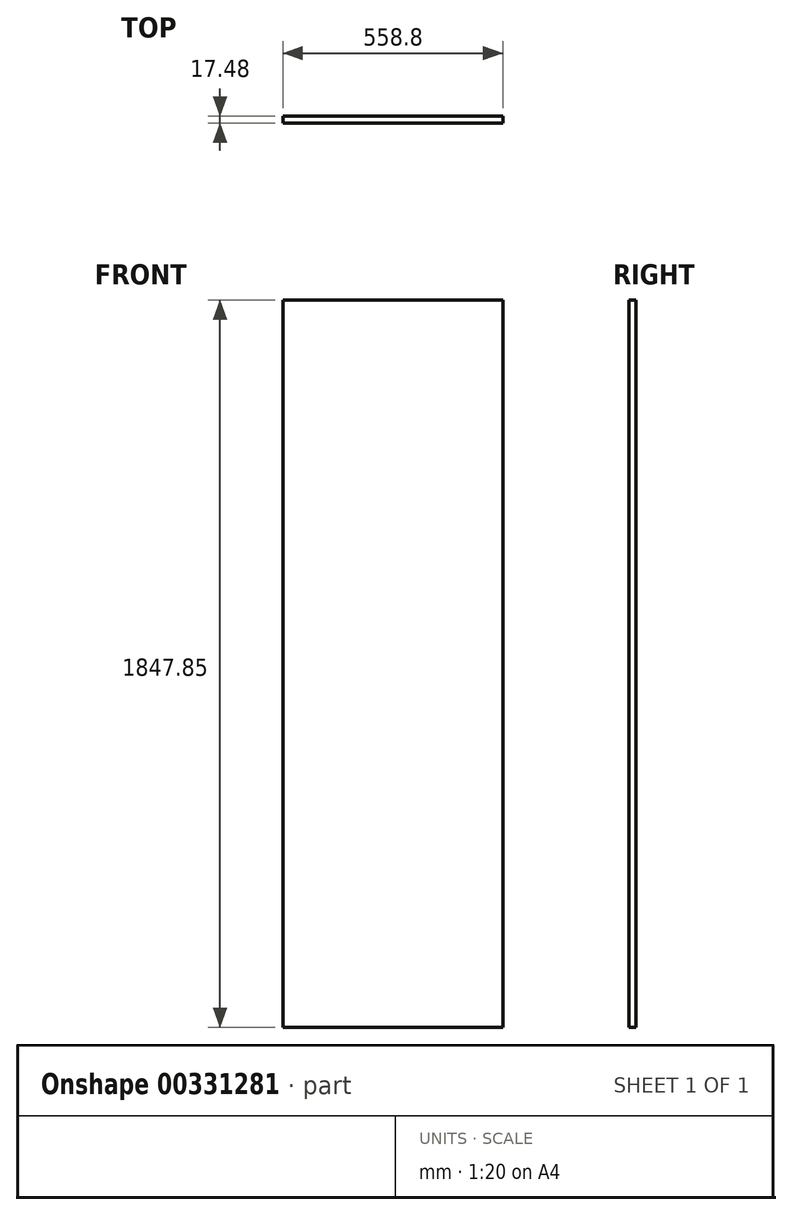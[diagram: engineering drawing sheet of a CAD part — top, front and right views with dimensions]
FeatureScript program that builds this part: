
annotation { "Feature Type Name" : "Feature", "Feature Type Description" : "" }
export const myFeature = defineFeature(function(context is Context, id is Id, definition is map)
    precondition{}
    {
        {
            var Q0;
            Q0=qCreatedBy(makeId("Front.planeOp"),FACE);
            var sketch = newSketch(context, id + "F0", { "sketchPlane" : qUnion([Q0])});
            skLineSegment(sketch, "E0.bottom", {"start": v(0, 1949.1) * mm, "end": v(558.8, 1949.1) * mm});
            skLineSegment(sketch, "E0.top", {"start": v(0, 101.24) * mm, "end": v(558.8, 101.24) * mm});
            skLineSegment(sketch, "E0.left", {"start": v(0, 1949.1) * mm, "end": v(0, 101.24) * mm});
            skLineSegment(sketch, "E0.right", {"start": v(558.8, 1949.1) * mm, "end": v(558.8, 101.24) * mm});
            skSolve(sketch);
        }
        {
            var Q0;
            Q0 = qSketchRegion(id + "F0", true);
            extrude(context, id + "F1", {"entities" : qUnion([Q0]), "depth" : 17.48 * mm});
        }
    });
